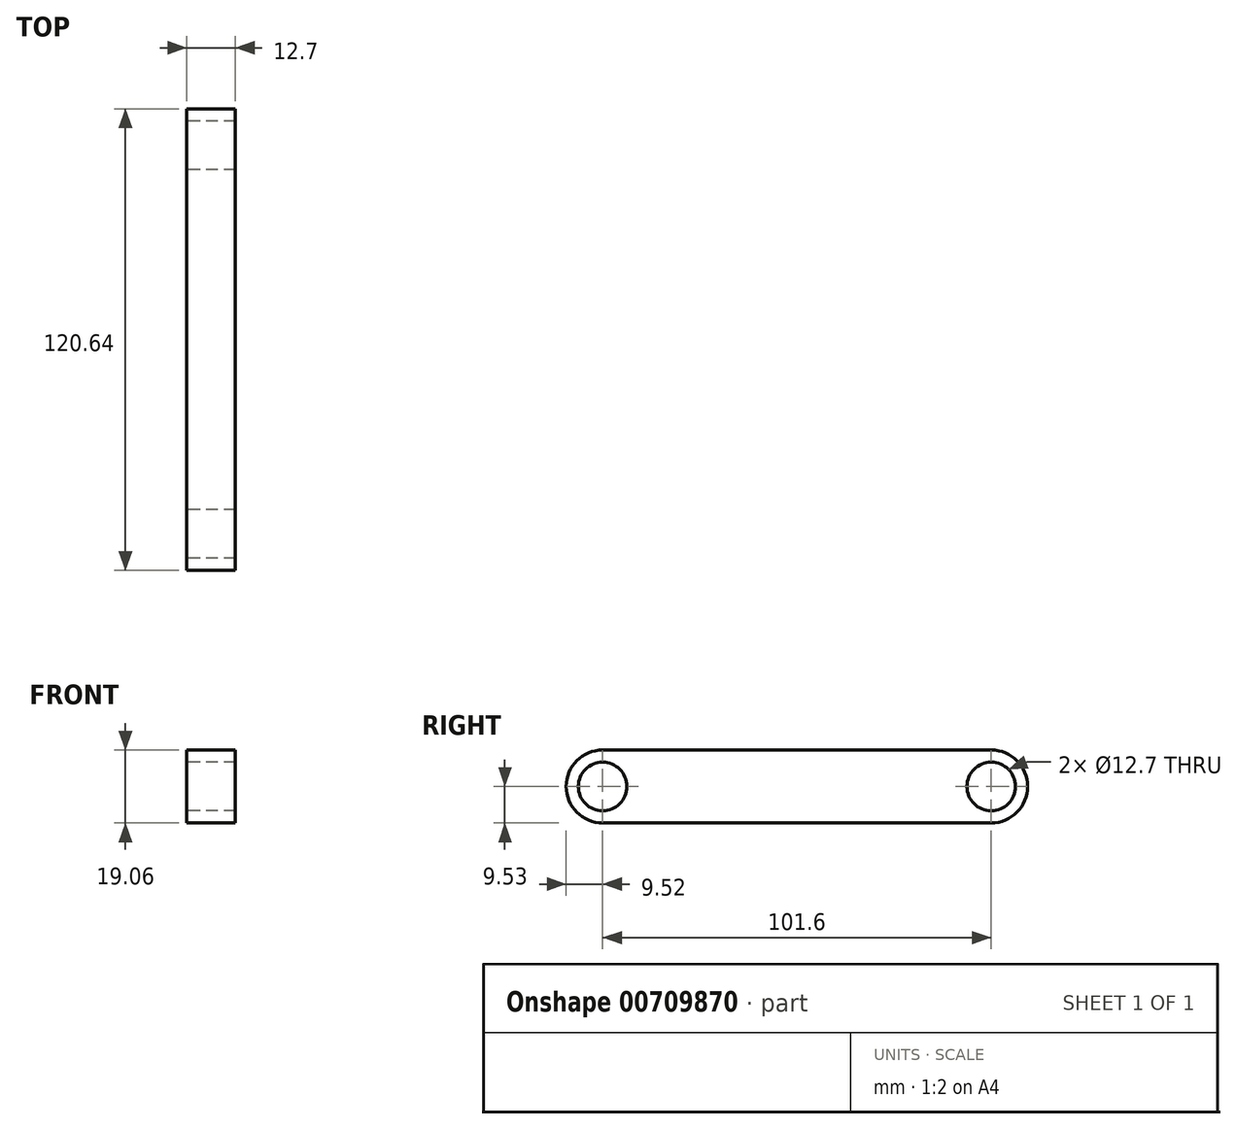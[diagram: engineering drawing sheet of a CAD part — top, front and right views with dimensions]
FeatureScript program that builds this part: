
annotation { "Feature Type Name" : "Feature", "Feature Type Description" : "" }
export const myFeature = defineFeature(function(context is Context, id is Id, definition is map)
    precondition{}
    {
        {
            var Q0;
            Q0=qCreatedBy(makeId("Right.planeOp"),FACE);
            var sketch = newSketch(context, id + "F0", { "sketchPlane" : qUnion([Q0])});
            skLineSegment(sketch, "E0", {"start": v(-50.8, 0) * mm, "end": v(50.8, 0) * mm});
            skCircle(sketch, "E1", {"center": v(-50.8, 0) * mm, "radius": 6.35 * mm});
            skCircle(sketch, "E2", {"center": v(50.8, 0) * mm, "radius": 6.35 * mm});
            skCircle(sketch, "E3", {"center": v(50.8, 0) * mm, "radius": 9.53 * mm});
            skCircle(sketch, "E4", {"center": v(-50.8, 0) * mm, "radius": 9.53 * mm});
            skLineSegment(sketch, "E5", {"start": v(-50.8, 9.53) * mm, "end": v(50.8, 9.53) * mm});
            skLineSegment(sketch, "E6", {"start": v(50.8, 9.53) * mm, "end": v(50.8, -9.53) * mm});
            skLineSegment(sketch, "E7", {"start": v(50.8, -9.53) * mm, "end": v(-50.8, -9.53) * mm});
            skSolve(sketch);
        }
        {
            var Q0;
            Q0=makeQuery(id+"F0.imprint","IMPRINT",FACE,{"disambiguationData":[TD([[makeQuery(id+"F0.imprint","IMPRINT",EDGE,{"derivedFrom":sQuery(id+"F0.wireOp",EDGE,"E1")}),-1.0]])]});
            var Q1;
            {var subQ5=sQuery(id+"F0.wireOp",EDGE,"E5");Q1=makeQuery(id+"F0.imprint","IMPRINT",FACE,{"disambiguationData":[TD([[makeQuery(id+"F0.imprint","IMPRINT",EDGE,{"derivedFrom":subQ5}),-1.0]])]});}
            var Q2;
            {var subQ0=sQuery(id+"F0.wireOp",EDGE,"E3");var subQ1=sQuery(id+"F0.wireOp",EDGE,"E0");var subQ2=makeQuery(id+"F0.imprint","INTERSECT",VERTEX,{"derivedFrom":[subQ1,subQ0]});Q2=makeQuery(id+"F0.imprint","IMPRINT",FACE,{"disambiguationData":[TD([[makeQuery(id+"F0.imprint","IMPRINT",EDGE,{"disambiguationData":[TD([[subQ2,-1.0]])],"derivedFrom":subQ1}),1.0]])]});}
            var Q3;
            {var subQ0=sQuery(id+"F0.wireOp",EDGE,"E6");var subQ1=sQuery(id+"F0.wireOp",EDGE,"E2");var subQ2=makeQuery(id+"F0.imprint","INTERSECT",VERTEX,{"disambiguationData":[OD(0.0)],"derivedFrom":[subQ1,subQ0]});Q3=makeQuery(id+"F0.imprint","IMPRINT",FACE,{"disambiguationData":[TD([[makeQuery(id+"F0.imprint","IMPRINT",EDGE,{"disambiguationData":[TD([[subQ2,1.0]])],"derivedFrom":subQ1}),-1.0]])]});}
            var Q4;
            {var subQ0=sQuery(id+"F0.wireOp",EDGE,"E3");var subQ1=sQuery(id+"F0.wireOp",EDGE,"E0");var subQ2=makeQuery(id+"F0.imprint","INTERSECT",VERTEX,{"derivedFrom":[subQ1,subQ0]});Q4=makeQuery(id+"F0.imprint","IMPRINT",FACE,{"disambiguationData":[TD([[makeQuery(id+"F0.imprint","IMPRINT",EDGE,{"disambiguationData":[TD([[subQ2,-1.0]])],"derivedFrom":subQ1}),-1.0]])]});}
            var Q5;
            {var subQ5=sQuery(id+"F0.wireOp",EDGE,"E7");Q5=makeQuery(id+"F0.imprint","IMPRINT",FACE,{"disambiguationData":[TD([[makeQuery(id+"F0.imprint","IMPRINT",EDGE,{"derivedFrom":subQ5}),-1.0]])]});}
            extrude(context, id + "F1", {"entities" : qUnion([Q0, Q1, Q2, Q3, Q4, Q5]), "endBound" : BoundingType.SYMMETRIC, "depth" : 12.7 * mm, "offsetDistance" : 25.4 * mm});
        }
    });
